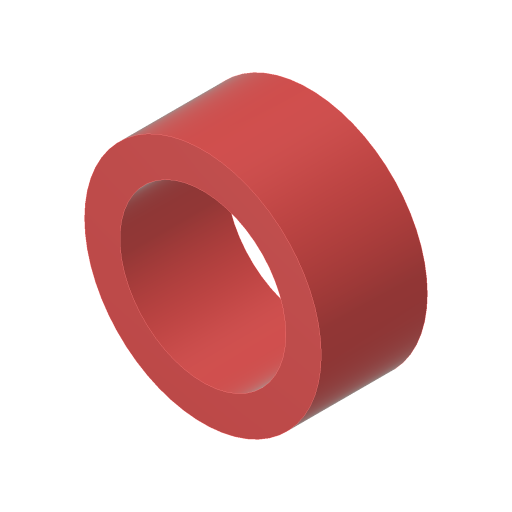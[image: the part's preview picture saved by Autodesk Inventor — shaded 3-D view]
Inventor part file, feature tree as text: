
AUTODESK INVENTOR PART (.ipt)
format: ipt  version: 2023.4 (Build 274418000, 418)  size: 117,760 bytes
history: native  units: in
note: dims shown in document units (in); Inventor stores cm internally (conversion verified against a paired STEP export)
features: extrude x1, sketch x1
ambient origin geometry x8: Origin, YZ Plane, XZ Plane, XY Plane, X Axis, Y Axis, Z Axis, Center Point
bodies: Solid1 (feature_tree)
feature tree (2):
  extrude  "Extrusion1"  Depth=0.3745in
  sketch  "Sketch1"  dims[d0=0.585in d1=0.125in d2=0.3745in d3=0.0in]
